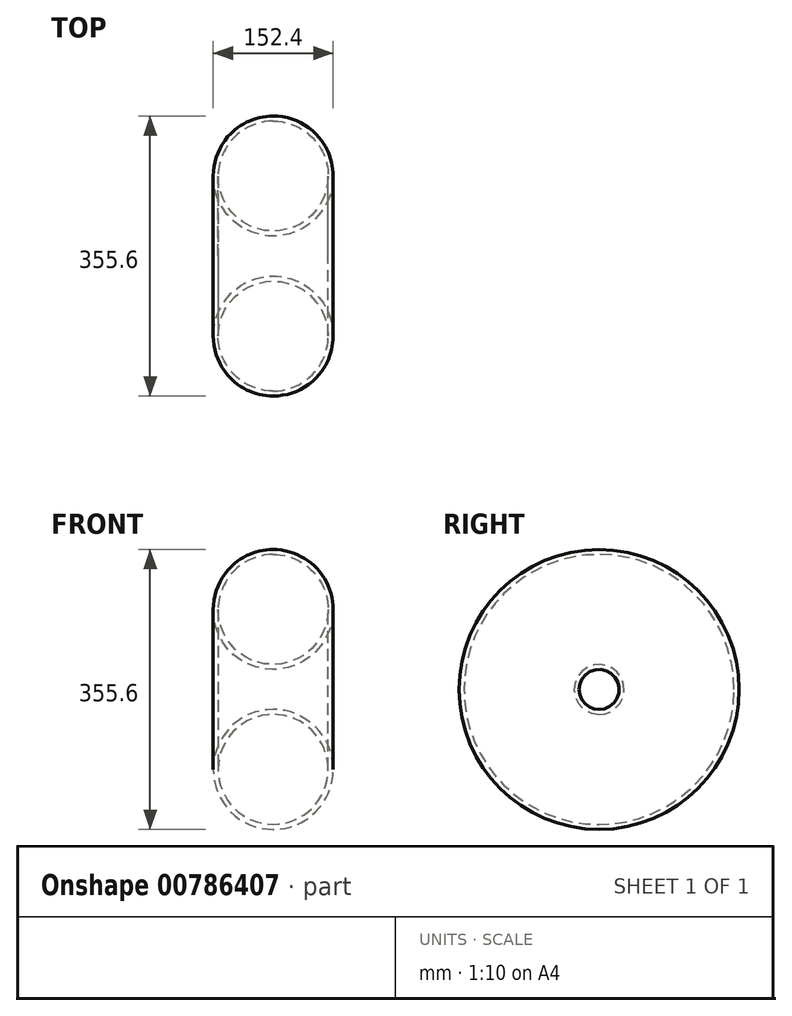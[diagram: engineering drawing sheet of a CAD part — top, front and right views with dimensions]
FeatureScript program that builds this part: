
annotation { "Feature Type Name" : "Feature", "Feature Type Description" : "" }
export const myFeature = defineFeature(function(context is Context, id is Id, definition is map)
    precondition{}
    {
        {
            var Q0;
            Q0=qCreatedBy(makeId("Top.planeOp"),FACE);
            var sketch = newSketch(context, id + "F0", { "sketchPlane" : qUnion([Q0])});
            skCircle(sketch, "E0", {"center": v(0, 101.6) * mm, "radius": 76.2 * mm});
            skCircle(sketch, "E1", {"center": v(0, 101.6) * mm, "radius": 69.85 * mm});
            skSolve(sketch);
        }
        {
            var Q0;
            Q0=qCreatedBy(makeId("Top.planeOp"),FACE);
            var sketch = newSketch(context, id + "F1", { "sketchPlane" : qUnion([Q0])});
            skLineSegment(sketch, "E2", {"start": v(0, 0) * mm, "end": v(-78.28, 0) * mm, "construction": true});
            skSolve(sketch);
        }
        {
            var Q0;
            Q0 = qSketchRegion(id + "F1", true);
            var Q1;
            Q1=makeQuery(id+"F0.imprint","IMPRINT",FACE,{"disambiguationData":[TD([[makeQuery(id+"F0.imprint","IMPRINT",EDGE,{"derivedFrom":sQuery(id+"F0.wireOp",EDGE,"E0")}),1.0]])]});
            var Q2;
            Q2=sQuery(id+"F1.wireOp",EDGE,"E2");
            revolve(context, id + "F2", {"surfaceOperationType" : NewSurfaceOperationType.NEW, "entities" : qUnion([Q0, Q1]), "axis" : qUnion([Q2]), "revolveType" : RevolveType.FULL});
        }
    });
